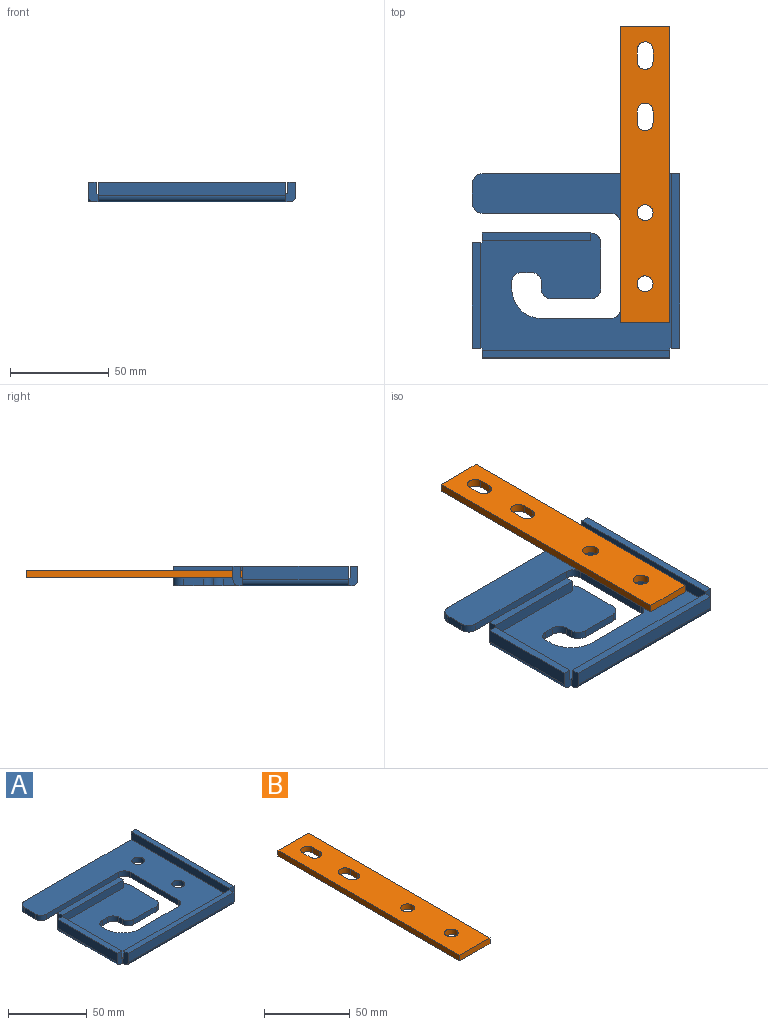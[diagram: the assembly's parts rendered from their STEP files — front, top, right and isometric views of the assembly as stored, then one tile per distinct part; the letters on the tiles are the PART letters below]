
ASSEMBLY  parts=2 mates=1
PART A: 47 faces, bbox 105x93.3x10 mm
  f0: plane 101x89.28mm, normal (0,0,1), area 6663.6mm2, adj f1,f2,f3,f4,f5,f6,f7,f8
  f1: cylinder r=5mm len=5.72mm, axis (0,0,-1), area 34.3mm2, adj f0,f2,f32,f33
  f2: plane 5x4mm, normal (0,-1,0), area 20mm2, adj f0,f1,f3,f33
  f3: cylinder r=5mm len=5mm, axis (0,0,-1), area 31.4mm2, adj f0,f2,f4,f33
  f4: plane 4x3.28mm, normal (-1,0,0), area 13.1mm2, adj f0,f3,f5,f33
  f5: cylinder r=5mm len=5mm, axis (0,0,-1), area 31.4mm2, adj f0,f4,f6,f33
  f6: plane 20.05x4mm, normal (0,-1,0), area 80.2mm2, adj f0,f5,f7,f33
  f7: cylinder r=5mm len=5mm, axis (0,0,-1), area 31.4mm2, adj f0,f6,f8,f33
  f8: plane 23.28x4mm, normal (1,0,0), area 93.1mm2, adj f0,f7,f9,f33
  f9: cylinder r=5mm len=5mm, axis (0,0,-1), area 24.9mm2, adj f0,f8,f10,f33,f46
  f10: plane 55x7mm, normal (0,1,0), area 385mm2, adj f9,f11,f39,f40,f46
  f11: plane 10x5mm, normal (-1,0,0), area 42.1mm2, adj f0,f10,f12,f33,f38,f40,f46
  f12: plane 10x5mm, normal (0,1,0), area 42.1mm2, adj f0,f11,f13,f33,f36,f37,f45
  f13: plane 53.28x7mm, normal (-1,0,0), area 372.9mm2, adj f12,f14,f37,f45
  f14: plane 10x5mm, normal (0,-1,0), area 42.1mm2, adj f0,f13,f15,f33,f36,f37,f45
  f15: plane 10x5mm, normal (-1,0,0), area 42.1mm2, adj f0,f14,f16,f33,f34,f35,f44
  f16: plane 95x7mm, normal (0,-1,0), area 665mm2, adj f15,f17,f35,f44
  f17: plane 10x5mm, normal (1,0,0), area 42.1mm2, adj f0,f16,f18,f33,f34,f35,f44
  f18: plane 10x5mm, normal (0,-1,0), area 42.1mm2, adj f0,f17,f19,f33,f41,f42,f43
  f19: plane 88.28x7mm, normal (1,0,0), area 617.9mm2, adj f18,f20,f42,f43
  f20: plane 100x10mm, normal (0,1,0), area 422.1mm2, adj f0,f19,f21,f33,f41,f42,f43
  f21: cylinder r=5mm len=5mm, axis (0,0,-1), area 31.4mm2, adj f0,f20,f22,f33
  f22: plane 10x4mm, normal (-1,0,0), area 40mm2, adj f0,f21,f23,f33
  f23: cylinder r=5mm len=5mm, axis (0,0,-1), area 31.4mm2, adj f0,f22,f24,f33
  f24: plane 65x4mm, normal (0,-1,0), area 260mm2, adj f0,f23,f25,f33
  f25: cylinder r=5mm len=5mm, axis (0,0,-1), area 31.4mm2, adj f0,f24,f26,f33
  f26: plane 43.28x4mm, normal (-1,0,0), area 173.1mm2, adj f0,f25,f27,f33
  f27: cylinder r=5mm len=5mm, axis (0,0,-1), area 31.4mm2, adj f0,f26,f28,f33
  f28: plane 35x4mm, normal (0,1,0), area 140mm2, adj f0,f27,f29,f33
  f29: cylinder r=15mm len=15mm, axis (0,0,-1), area 94.2mm2, adj f0,f28,f32,f33
  f30: cylinder r=4mm len=8mm, axis (0,0,-1), area 100.5mm2, adj f0,f33
  f31: cylinder r=4mm len=8mm, axis (0,0,-1), area 100.5mm2, adj f0,f33
  f32: plane 4x2.56mm, normal (1,0,0), area 10.2mm2, adj f0,f1,f29,f33
  f33: plane 102x90.28mm, normal (0,0,-1), area 6945.2mm2, adj f1,f2,f3,f4,f5,f6,f7,f8
  f34: plane 95x6mm, normal (0,1,0), area 570mm2, adj f0,f15,f17,f35
  f35: plane 95x4mm, normal (0,0,1), area 380mm2, adj f15,f16,f17,f34
  f36: plane 53.28x6mm, normal (1,0,0), area 319.6mm2, adj f0,f12,f14,f37
  f37: plane 53.28x4mm, normal (0,0,1), area 213.1mm2, adj f12,f13,f14,f36
  f38: plane 55x6mm, normal (0,-1,0), area 330mm2, adj f0,f11,f39,f40
  f39: plane 6x4mm, normal (1,0,0), area 24mm2, adj f0,f10,f38,f40
  f40: plane 55x4mm, normal (0,0,1), area 220mm2, adj f10,f11,f38,f39
  f41: plane 88.28x6mm, normal (-1,0,0), area 529.6mm2, adj f0,f18,f20,f42
  f42: plane 88.28x4mm, normal (0,0,1), area 353.1mm2, adj f18,f19,f20,f41
  f43: cylinder r=3mm len=88.28mm, axis (0,1,0), area 416mm2, adj f18,f19,f20,f33
  f44: cylinder r=3mm len=95mm, axis (1,0,0), area 447.7mm2, adj f15,f16,f17,f33
  f45: cylinder r=3mm len=53.28mm, axis (0,-1,0), area 251.1mm2, adj f12,f13,f14,f33
  f46: cylinder r=3mm len=59.58mm, axis (-1,0,0), area 271.7mm2, adj f9,f10,f11,f33
PART B: 16 faces, bbox 25x150x4 mm
  f0: plane 25x4mm, normal (0,1,0), area 100mm2, adj f1,f13,f14,f15
  f1: plane 150x4mm, normal (-1,0,0), area 600mm2, adj f0,f2,f14,f15
  f2: plane 25x4mm, normal (0,-1,0), area 100mm2, adj f1,f13,f14,f15
  f3: cylinder r=4mm len=8mm, axis (0,0,-1), area 50.3mm2, adj f4,f9,f14,f15
  f4: plane 6x4mm, normal (1,0,0), area 24mm2, adj f3,f5,f14,f15
  f5: cylinder r=4mm len=8mm, axis (0,0,-1), area 50.3mm2, adj f4,f9,f14,f15
  f6: cylinder r=4mm len=8mm, axis (0,0,-1), area 50.3mm2, adj f7,f12,f14,f15
  f7: plane 6x4mm, normal (1,0,0), area 24mm2, adj f6,f8,f14,f15
  f8: cylinder r=4mm len=8mm, axis (0,0,-1), area 50.3mm2, adj f7,f12,f14,f15
  f9: plane 6x4mm, normal (-1,0,0), area 24mm2, adj f3,f5,f14,f15
  f10: cylinder r=4mm len=8mm, axis (0,0,-1), area 100.5mm2, adj f14,f15
  f11: cylinder r=4mm len=8mm, axis (0,0,-1), area 100.5mm2, adj f14,f15
  f12: plane 6x4mm, normal (-1,0,0), area 24mm2, adj f6,f8,f14,f15
  f13: plane 150x4mm, normal (1,0,0), area 600mm2, adj f0,f2,f14,f15
  f14: plane 150x25mm, normal (0,0,1), area 3452.9mm2, adj f0,f1,f2,f3,f4,f5,f6,f7
  f15: plane 150x25mm, normal (0,0,-1), area 3452.9mm2, adj f0,f1,f2,f3,f4,f5,f6,f7
PLACE A t=(-35.09,-32.99,10.94)mm
PLACE B t=(20.68,-11.98,14.94)mm
MATE revolute A.f30 <-> B.f10  axis (0,0,1) through (17.46,-40.98,14.94)mm
